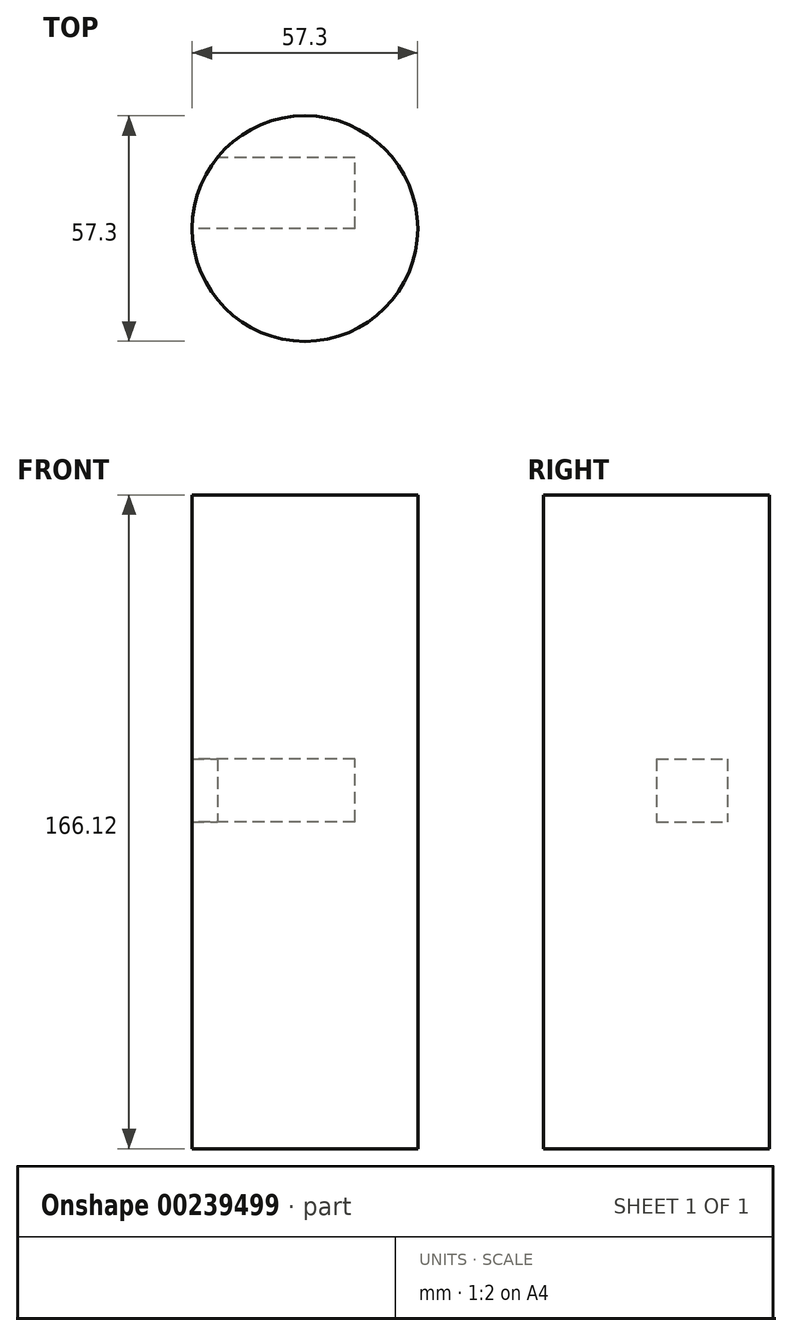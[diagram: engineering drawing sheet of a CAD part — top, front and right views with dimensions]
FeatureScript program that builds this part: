
annotation { "Feature Type Name" : "Feature", "Feature Type Description" : "" }
export const myFeature = defineFeature(function(context is Context, id is Id, definition is map)
    precondition{}
    {
        {
            var Q0;
            Q0=qCreatedBy(makeId("Top.planeOp"),FACE);
            var sketch = newSketch(context, id + "F0", { "sketchPlane" : qUnion([Q0])});
            skCircle(sketch, "E0", {"center": v(0, 0) * mm, "radius": 28.65 * mm});
            skSolve(sketch);
        }
        {
            var Q0;
            Q0 = qSketchRegion(id + "F0", true);
            extrude(context, id + "F1", {"entities" : qUnion([Q0]), "endBound" : BoundingType.SYMMETRIC, "depth" : 166.12 * mm});
        }
        {
            var Q0;
            Q0=qCreatedBy(makeId("Right.planeOp"),FACE);
            var sketch = newSketch(context, id + "F2", { "sketchPlane" : qUnion([Q0])});
            skLineSegment(sketch, "E1.bottom", {"start": v(0, 0) * mm, "end": v(18.06, 0) * mm});
            skLineSegment(sketch, "E1.top", {"start": v(0, 15.95) * mm, "end": v(18.06, 15.95) * mm});
            skLineSegment(sketch, "E1.left", {"start": v(0, 0) * mm, "end": v(0, 15.95) * mm});
            skLineSegment(sketch, "E1.right", {"start": v(18.06, 0) * mm, "end": v(18.06, 15.95) * mm});
            skSolve(sketch);
        }
        {
            var Q0;
            Q0 = qSketchRegion(id + "F2", true);
            extrude(context, id + "F3", {"entities" : qUnion([Q0]), "operationType" : NewBodyOperationType.REMOVE, "endBound" : BoundingType.SYMMETRIC, "depth" : 25.4 * mm});
        }
        {
            var Q0;
            Q0 = qSketchRegion(id + "F2", true);
            extrude(context, id + "F4", {"entities" : qUnion([Q0]), "operationType" : NewBodyOperationType.REMOVE, "oppositeDirection" : true, "depth" : 60.7 * mm});
        }
    });
